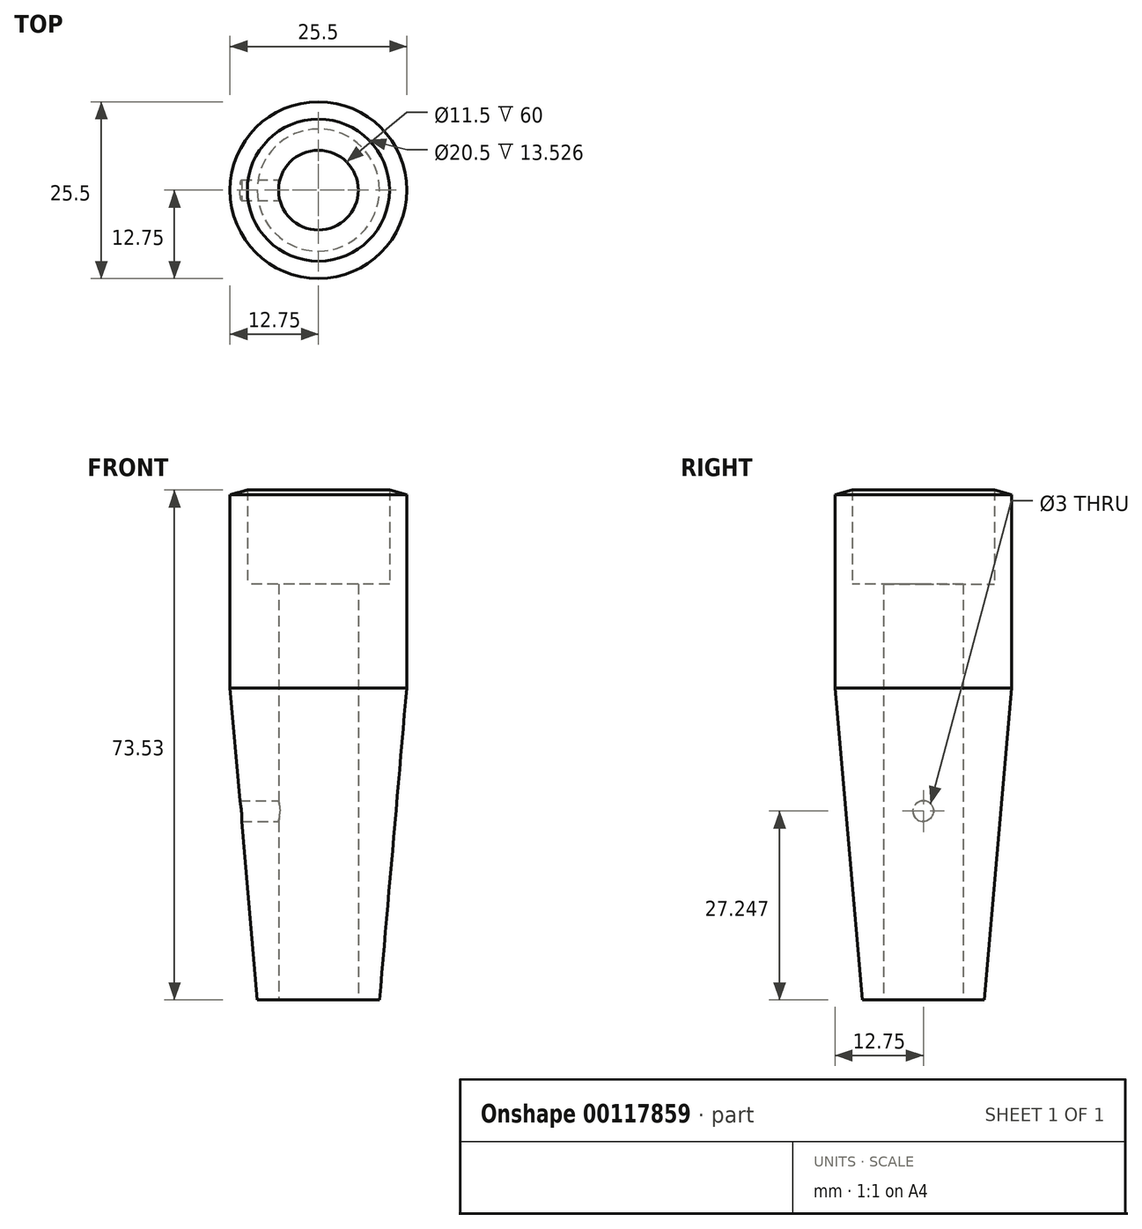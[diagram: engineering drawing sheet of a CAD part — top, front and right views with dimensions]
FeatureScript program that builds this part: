
annotation { "Feature Type Name" : "Feature", "Feature Type Description" : "" }
export const myFeature = defineFeature(function(context is Context, id is Id, definition is map)
    precondition{}
    {
        {
            var Q0;
            Q0=qCreatedBy(makeId("Top.planeOp"),FACE);
            var sketch = newSketch(context, id + "F0", { "sketchPlane" : qUnion([Q0])});
            skCircle(sketch, "E0", {"center": v(0, 0) * mm, "radius": 5.75 * mm});
            skCircle(sketch, "E1", {"center": v(0, 0) * mm, "radius": 10.25 * mm});
            skCircle(sketch, "E2", {"center": v(0, 0) * mm, "radius": 12.75 * mm});
            skSolve(sketch);
        }
        {
            var Q0;
            Q0=makeQuery(id+"F0.imprint","IMPRINT",FACE,{"disambiguationData":[TD([[makeQuery(id+"F0.imprint","IMPRINT",EDGE,{"derivedFrom":sQuery(id+"F0.wireOp",EDGE,"E0")}),-1.0]])]});
            extrude(context, id + "F1", {"entities" : qUnion([Q0]), "depth" : 20 * mm});
        }
        {
            var Q0;
            Q0 = qSketchRegion(id + "F0", true);
            extrude(context, id + "F2", {"entities" : qUnion([Q0]), "operationType" : NewBodyOperationType.ADD, "depth" : 35 * mm});
        }
        {
            var Q0;
            {var subQ0=sQuery(id+"F0.wireOp",EDGE,"E1");Q0=makeQuery(id+"F2.boolean.opBoolean","MERGE",FACE,{"derivedFrom":[makeQuery(id+"F1.opExtrude","CAP_FACE",FACE,{"disambiguationData":[OSD([sQuery(id+"F0.wireOp",EDGE,"E0"),subQ0])],"isStart":true}),makeQuery(id+"F2.opExtrude","CAP_FACE",FACE,{"disambiguationData":[OSD([subQ0,sQuery(id+"F0.wireOp",EDGE,"E2")])],"isStart":true})]});}
            extrude(context, id + "F3", {"entities" : qUnion([Q0]), "operationType" : NewBodyOperationType.ADD, "depth" : 40 * mm});
        }
        {
            var Q0;
            Q0=makeQuery(id+"F2.opExtrude","CAP_EDGE",EDGE,{"disambiguationData":[OSD([sQuery(id+"F0.wireOp",EDGE,"E2")])],"isStart":false});
            chamfer(context, id + "F4", {"entities" : qUnion([Q0]), "chamferType" : ChamferType.OFFSET_ANGLE, "width" : 8 * mm, "oppositeDirection" : false, "angle" : 15 * degree});
        }
        {
            var Q0;
            Q0=makeQuery(id+"F3.opExtrude","CAP_EDGE",EDGE,{"disambiguationData":[OSD([sQuery(id+"F0.wireOp",EDGE,"E2")])],"isStart":false});
            chamfer(context, id + "F5", {"entities" : qUnion([Q0]), "chamferType" : ChamferType.OFFSET_ANGLE, "width" : 45 * mm, "oppositeDirection" : false, "angle" : 5 * degree, "tangentPropagation" : true});
        }
        {
            var Q0;
            Q0=qCreatedBy(makeId("Right.planeOp"),FACE);
            var sketch = newSketch(context, id + "F6", { "sketchPlane" : qUnion([Q0])});
            skLineSegment(sketch, "E3", {"start": v(0, -25.5) * mm, "end": v(0, 0) * mm});
            skCircle(sketch, "E4", {"center": v(0, -12.75) * mm, "radius": 1.5 * mm});
            skSolve(sketch);
        }
        {
            var Q0;
            Q0 = qSketchRegion(id + "F6", true);
            extrude(context, id + "F7", {"entities" : qUnion([Q0]), "operationType" : NewBodyOperationType.REMOVE, "oppositeDirection" : true, "depth" : 25 * mm});
        }
    });
